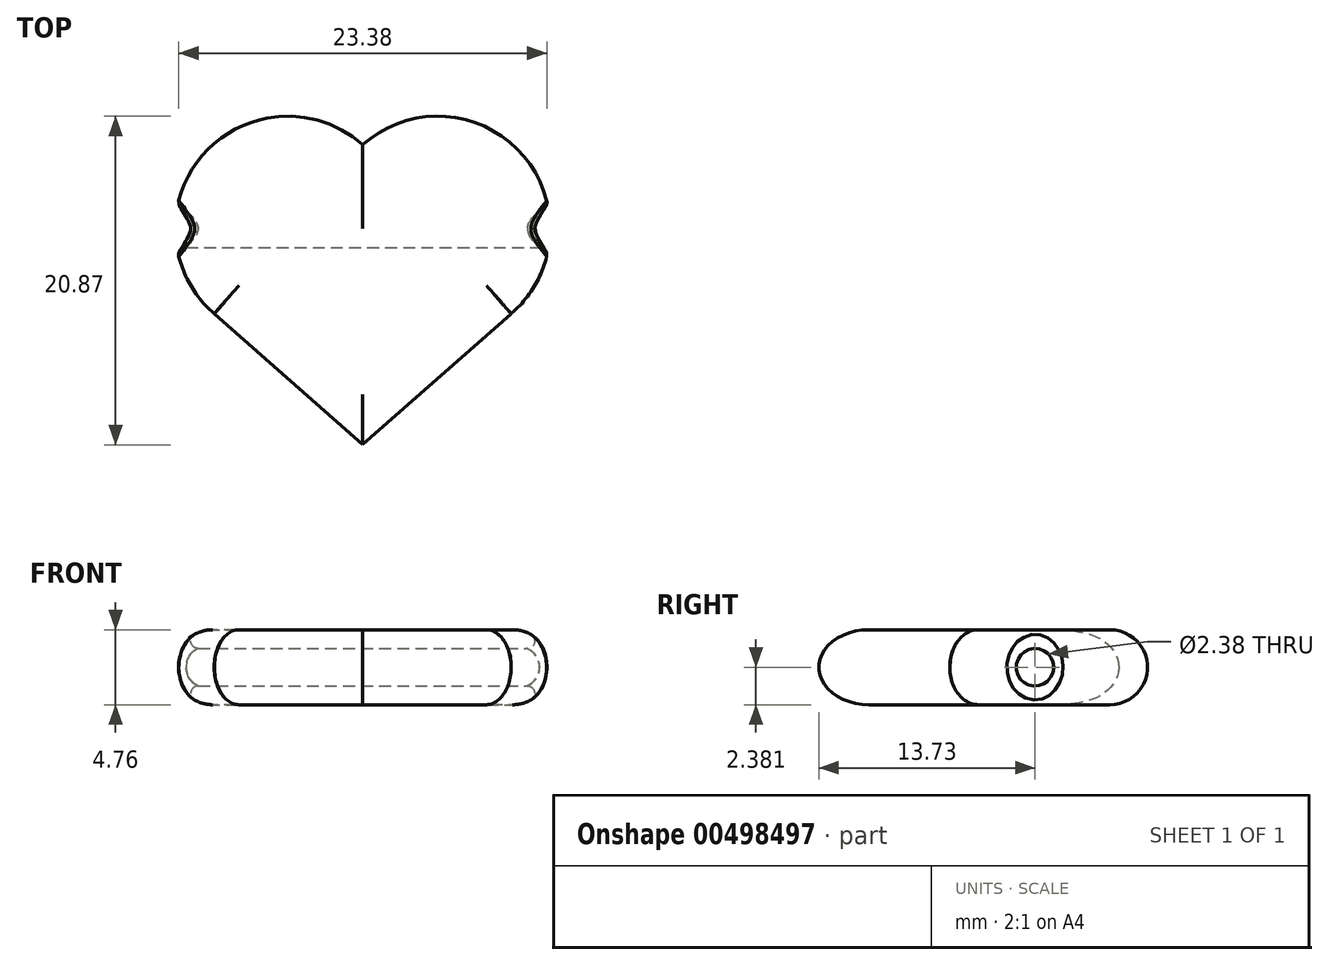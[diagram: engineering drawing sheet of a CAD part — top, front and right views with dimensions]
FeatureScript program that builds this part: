
annotation { "Feature Type Name" : "Feature", "Feature Type Description" : "" }
export const myFeature = defineFeature(function(context is Context, id is Id, definition is map)
    precondition{}
    {
        {
            var Q0;
            Q0=qCreatedBy(makeId("Top.planeOp"),FACE);
            var sketch = newSketch(context, id + "F0", { "sketchPlane" : qUnion([Q0])});
            skArc(sketch, "E0", {"start": v(0, 7.1) * mm, "mid": v(-13.5, 6.29) * mm, "end": v(-12.57, -7.21) * mm});
            skArc(sketch, "E1", {"start": v(0, 7.1) * mm, "mid": v(13.5, 6.29) * mm, "end": v(12.57, -7.21) * mm});
            skLineSegment(sketch, "E2", {"start": v(-12.57, -7.21) * mm, "end": v(0, -18.3) * mm});
            skLineSegment(sketch, "E3", {"start": v(0, -18.3) * mm, "end": v(12.57, -7.21) * mm});
            skSolve(sketch);
        }
        {
            var Q0;
            Q0=makeQuery(id+"F0.imprint","IMPRINT",FACE,{"disambiguationData":[TD([[makeQuery(id+"F0.imprint","IMPRINT",EDGE,{"derivedFrom":sQuery(id+"F0.wireOp",EDGE,"E0")}),1.0]])]});
            extrude(context, id + "F1", {"entities" : qUnion([Q0]), "depth" : 6.35 * mm});
        }
        {
            var Q0;
            Q0=makeQuery(id+"F1.opExtrude","CAP_FACE",FACE,{"disambiguationData":[OSD([sQuery(id+"F0.wireOp",EDGE,"E0"),sQuery(id+"F0.wireOp",EDGE,"E1"),sQuery(id+"F0.wireOp",EDGE,"E2"),sQuery(id+"F0.wireOp",EDGE,"E3")])],"isStart":false});
            var Q1;
            Q1=makeQuery(id+"F1.opExtrude","CAP_FACE",FACE,{"disambiguationData":[OSD([sQuery(id+"F0.wireOp",EDGE,"E0"),sQuery(id+"F0.wireOp",EDGE,"E1"),sQuery(id+"F0.wireOp",EDGE,"E2"),sQuery(id+"F0.wireOp",EDGE,"E3")])],"isStart":true});
            fillet(context, id + "F2", {"entities" : qUnion([Q0, Q1]), "radius" : 3.17 * mm, "tangentPropagation" : true, "allowEdgeOverflow" : false});
        }
        {
            var Q0;
            Q0=makeQuery(id+"F2.opFillet","BLEND_EDGE",EDGE,{"blendedFrom":[makeQuery(id+"F1.opExtrude","CAP_EDGE",EDGE,{"disambiguationData":[OSD([sQuery(id+"F0.wireOp",EDGE,"E0")])],"isStart":false}),makeQuery(id+"F1.opExtrude","CAP_EDGE",EDGE,{"disambiguationData":[OSD([sQuery(id+"F0.wireOp",EDGE,"E2")])],"isStart":false})],"blendedInto":[]});
            var Q1;
            Q1=makeQuery(id+"F2.opFillet","BLEND_EDGE",EDGE,{"blendedFrom":[makeQuery(id+"F1.opExtrude","CAP_EDGE",EDGE,{"disambiguationData":[OSD([sQuery(id+"F0.wireOp",EDGE,"E1")])],"isStart":false}),makeQuery(id+"F1.opExtrude","CAP_EDGE",EDGE,{"disambiguationData":[OSD([sQuery(id+"F0.wireOp",EDGE,"E3")])],"isStart":false})],"blendedInto":[]});
            fillet(context, id + "F3", {"entities" : qUnion([Q0, Q1]), "radius" : 2.54 * mm, "tangentPropagation" : true, "allowEdgeOverflow" : false});
        }
        {
            var Q0;
            Q0=qCreatedBy(makeId("Right.planeOp"),FACE);
            var sketch = newSketch(context, id + "F4", { "sketchPlane" : qUnion([Q0])});
            skCircle(sketch, "E4", {"center": v(0, 3.18) * mm, "radius": 1.59 * mm});
            skSolve(sketch);
        }
        {
            var Q0;
            Q0 = qSketchRegion(id + "F4", true);
            extrude(context, id + "F5", {"entities" : qUnion([Q0]), "operationType" : NewBodyOperationType.REMOVE, "endBound" : BoundingType.SYMMETRIC, "oppositeDirection" : true, "depth" : 50.8 * mm});
        }
        {
            var Q0;
            Q0=makeQuery(id+"F5.boolean.opBoolean","INTERSECT",EDGE,{"derivedFrom":[makeQuery(id+"F2.opFillet","BLEND_FACE",FACE,{"disambiguationData":[OSD([sQuery(id+"F0.wireOp",EDGE,"E1")])]}),makeQuery(id+"F5.opExtrude","SWEPT_FACE",FACE,{"disambiguationData":[OSD([sQuery(id+"F4.wireOp",EDGE,"E4")])]})]});
            var Q1;
            Q1=makeQuery(id+"F5.boolean.opBoolean","INTERSECT",EDGE,{"derivedFrom":[makeQuery(id+"F2.opFillet","BLEND_FACE",FACE,{"disambiguationData":[OSD([sQuery(id+"F0.wireOp",EDGE,"E0")])]}),makeQuery(id+"F5.opExtrude","SWEPT_FACE",FACE,{"disambiguationData":[OSD([sQuery(id+"F4.wireOp",EDGE,"E4")])]})]});
            fillet(context, id + "F6", {"entities" : qUnion([Q0, Q1]), "radius" : 0.64 * mm, "tangentPropagation" : true, "allowEdgeOverflow" : false});
        }
        {
            var Q0;
            Q0=makeQuery(id+"F1.opExtrude","SWEPT_BODY",BODY,{"disambiguationData":[OSD([sQuery(id+"F0.wireOp",EDGE,"E0"),sQuery(id+"F0.wireOp",EDGE,"E1"),sQuery(id+"F0.wireOp",EDGE,"E2"),sQuery(id+"F0.wireOp",EDGE,"E3")])]});
            var Q1;
            Q1=qCreatedBy(makeId("Origin.pointOp"),VERTEX);
            transform(context, id + "F7", {"entities" : qUnion([Q0]), "transformType" : TransformType.SCALE_UNIFORMLY, "scale" : .75, "scalePoint" : qUnion([Q1]), "makeCopy" : false});
        }
    });
